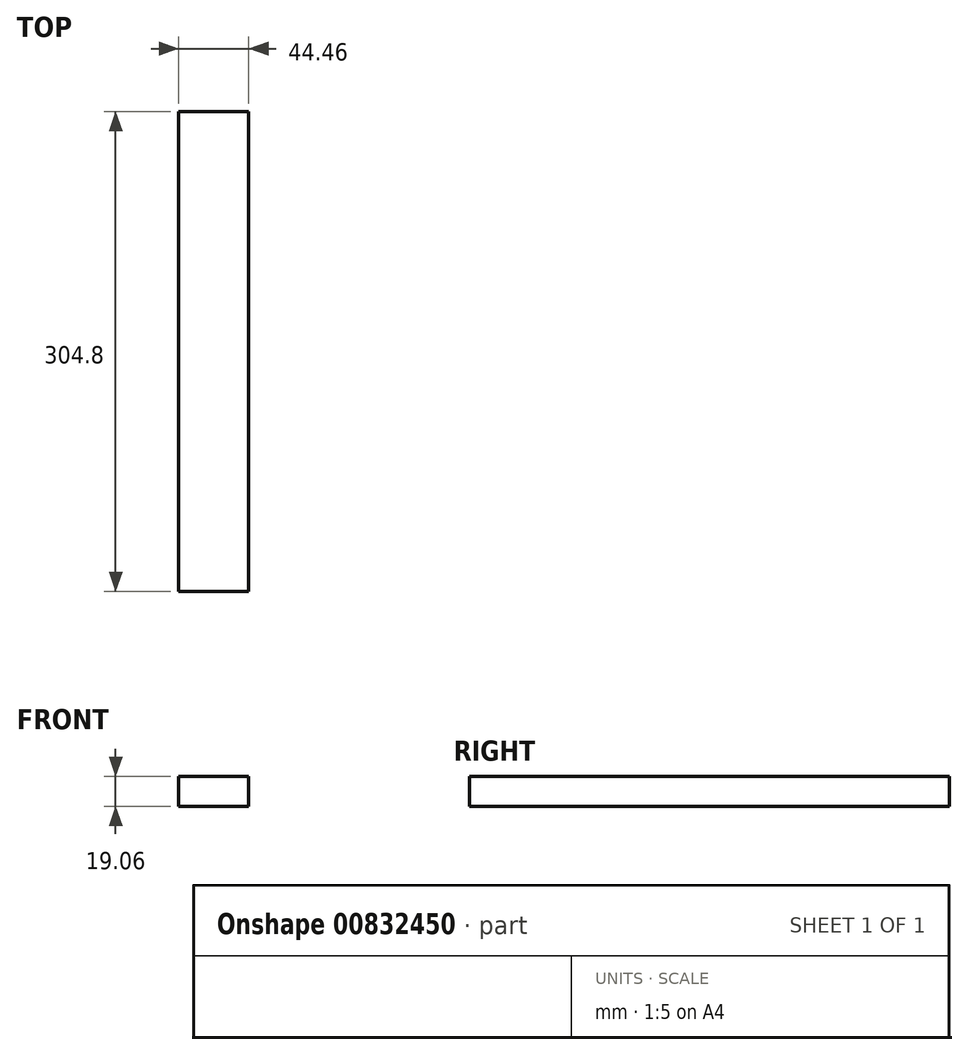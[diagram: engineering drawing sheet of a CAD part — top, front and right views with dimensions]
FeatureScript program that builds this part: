
annotation { "Feature Type Name" : "Feature", "Feature Type Description" : "" }
export const myFeature = defineFeature(function(context is Context, id is Id, definition is map)
    precondition{}
    {
        {
            var Q0;
            Q0=qCreatedBy(makeId("Front.planeOp"),FACE);
            var sketch = newSketch(context, id + "F0", { "sketchPlane" : qUnion([Q0])});
            skLineSegment(sketch, "E0.bottom", {"start": v(22.23, -9.52) * mm, "end": v(-22.23, -9.53) * mm});
            skLineSegment(sketch, "E0.top", {"start": v(22.23, 9.53) * mm, "end": v(-22.23, 9.52) * mm});
            skLineSegment(sketch, "E0.left", {"start": v(22.23, -9.52) * mm, "end": v(22.22, 9.53) * mm});
            skLineSegment(sketch, "E0.right", {"start": v(-22.23, -9.53) * mm, "end": v(-22.23, 9.52) * mm});
            skPoint(sketch, "E0.middle", {"position": v(0, 0) * mm});
            skSolve(sketch);
        }
        {
            var Q0;
            Q0=makeQuery(id+"F0.imprint","IMPRINT",FACE,{"disambiguationData":[TD([[makeQuery(id+"F0.imprint","IMPRINT",EDGE,{"derivedFrom":sQuery(id+"F0.wireOp",EDGE,"E0.bottom")}),-1.0]])]});
            extrude(context, id + "F1", {"entities" : qUnion([Q0]), "depth" : 304.8 * mm, "offsetDistance" : 25.4 * mm});
        }
    });
